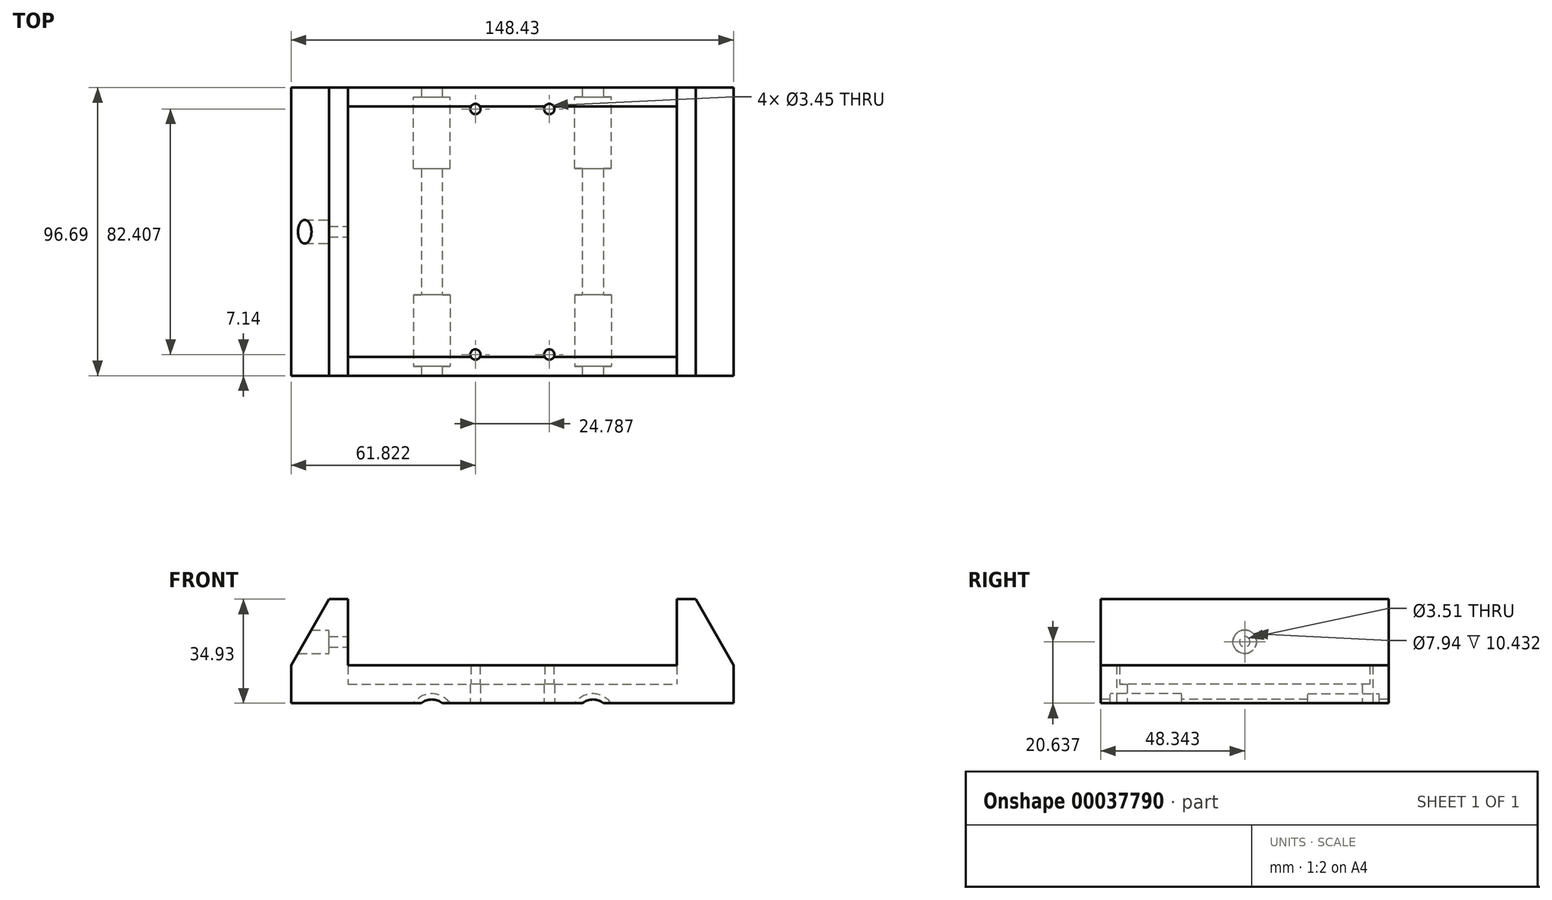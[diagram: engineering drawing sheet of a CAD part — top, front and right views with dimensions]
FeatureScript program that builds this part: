
annotation { "Feature Type Name" : "Feature", "Feature Type Description" : "" }
export const myFeature = defineFeature(function(context is Context, id is Id, definition is map)
    precondition{}
    {
        {
            var Q0;
            Q0=qCreatedBy(makeId("Top.planeOp"),FACE);
            var sketch = newSketch(context, id + "F0", { "sketchPlane" : qUnion([Q0])});
            skLineSegment(sketch, "E0.bottom", {"start": v(0, 0) * mm, "end": v(148.43, 0) * mm});
            skLineSegment(sketch, "E0.top", {"start": v(0, -96.7) * mm, "end": v(148.43, -96.7) * mm});
            skLineSegment(sketch, "E0.left", {"start": v(0, 0) * mm, "end": v(0, -96.7) * mm});
            skLineSegment(sketch, "E0.right", {"start": v(148.43, 0) * mm, "end": v(148.43, -96.7) * mm});
            skLineSegment(sketch, "E1", {"start": v(0, -48.35) * mm, "end": v(148.43, -48.35) * mm, "construction": true});
            skLineSegment(sketch, "E2.rect.bottom", {"start": v(61.82, -7.14) * mm, "end": v(86.6, -7.14) * mm, "construction": true});
            skLineSegment(sketch, "E2.rect.top", {"start": v(61.82, -89.55) * mm, "end": v(86.6, -89.55) * mm, "construction": true});
            skLineSegment(sketch, "E2.rect.left", {"start": v(61.82, -7.14) * mm, "end": v(61.82, -89.55) * mm, "construction": true});
            skLineSegment(sketch, "E2.rect.right", {"start": v(86.6, -7.14) * mm, "end": v(86.6, -89.55) * mm, "construction": true});
            skPoint(sketch, "E2.rect.middle", {"position": v(74.22, -48.35) * mm});
            skCircle(sketch, "E3", {"center": v(61.82, -7.14) * mm, "radius": 1.73 * mm});
            skCircle(sketch, "E4", {"center": v(86.6, -7.14) * mm, "radius": 1.73 * mm});
            skCircle(sketch, "E5", {"center": v(86.6, -89.55) * mm, "radius": 1.73 * mm});
            skCircle(sketch, "E6", {"center": v(61.82, -89.55) * mm, "radius": 1.73 * mm});
            skLineSegment(sketch, "E7", {"start": v(61.82, -7.14) * mm, "end": v(61.82, 0) * mm, "construction": true});
            skSolve(sketch);
        }
        {
            var Q0;
            Q0 = qSketchRegion(id + "F0", true);
            extrude(context, id + "F1", {"entities" : qUnion([Q0]), "depth" : 6.35 * mm});
        }
        {
            var Q0;
            Q0=makeQuery(id+"F1.opExtrude","CAP_FACE",FACE,{"disambiguationData":[OSD([sQuery(id+"F0.wireOp",EDGE,"E0.bottom"),sQuery(id+"F0.wireOp",EDGE,"E0.top"),sQuery(id+"F0.wireOp",EDGE,"E0.left"),sQuery(id+"F0.wireOp",EDGE,"E0.right")])],"isStart":false});
            var sketch = newSketch(context, id + "F2", { "sketchPlane" : qUnion([Q0])});
            skLineSegment(sketch, "E8.bottom", {"start": v(0, 0) * mm, "end": v(148.43, 0) * mm});
            skLineSegment(sketch, "E8.top", {"start": v(0, -96.7) * mm, "end": v(148.43, -96.7) * mm});
            skLineSegment(sketch, "E8.left", {"start": v(0, 0) * mm, "end": v(0, -96.7) * mm});
            skLineSegment(sketch, "E8.right", {"start": v(148.43, 0) * mm, "end": v(148.43, -96.7) * mm});
            skLineSegment(sketch, "E9.bottom", {"start": v(19.05, -6.35) * mm, "end": v(129.38, -6.35) * mm});
            skLineSegment(sketch, "E9.top", {"start": v(19.05, -90.34) * mm, "end": v(129.38, -90.34) * mm});
            skLineSegment(sketch, "E9.left", {"start": v(19.05, -6.35) * mm, "end": v(19.05, -90.34) * mm});
            skLineSegment(sketch, "E9.right", {"start": v(129.38, -6.35) * mm, "end": v(129.38, -90.34) * mm});
            skLineSegment(sketch, "E10", {"start": v(129.38, -48.35) * mm, "end": v(148.43, -48.35) * mm, "construction": true});
            skLineSegment(sketch, "E11", {"start": v(19.05, -48.35) * mm, "end": v(0, -48.35) * mm, "construction": true});
            skLineSegment(sketch, "E12", {"start": v(74.22, -6.35) * mm, "end": v(74.22, 0) * mm, "construction": true});
            skSolve(sketch);
        }
        {
            var Q0;
            Q0 = qSketchRegion(id + "F2", true);
            extrude(context, id + "F3", {"entities" : qUnion([Q0]), "operationType" : NewBodyOperationType.ADD, "depth" : 6.35 * mm});
        }
        {
            var Q0;
            Q0=makeQuery(id+"F3.opExtrude","CAP_FACE",FACE,{"disambiguationData":[OSD([sQuery(id+"F2.wireOp",EDGE,"E8.bottom"),sQuery(id+"F2.wireOp",EDGE,"E8.top"),sQuery(id+"F2.wireOp",EDGE,"E8.left"),sQuery(id+"F2.wireOp",EDGE,"E8.right"),sQuery(id+"F2.wireOp",EDGE,"E9.bottom"),sQuery(id+"F2.wireOp",EDGE,"E9.top"),sQuery(id+"F2.wireOp",EDGE,"E9.left"),sQuery(id+"F2.wireOp",EDGE,"E9.right")])],"isStart":false});
            var sketch = newSketch(context, id + "F4", { "sketchPlane" : qUnion([Q0])});
            skLineSegment(sketch, "E13.bottom", {"start": v(0, 0) * mm, "end": v(19.05, 0) * mm});
            skLineSegment(sketch, "E13.top", {"start": v(0, -96.7) * mm, "end": v(19.05, -96.7) * mm});
            skLineSegment(sketch, "E13.left", {"start": v(0, 0) * mm, "end": v(0, -96.7) * mm});
            skLineSegment(sketch, "E13.right", {"start": v(19.05, 0) * mm, "end": v(19.05, -96.7) * mm});
            skLineSegment(sketch, "E14.bottom", {"start": v(148.43, 0) * mm, "end": v(129.38, 0) * mm});
            skLineSegment(sketch, "E14.top", {"start": v(148.43, -96.7) * mm, "end": v(129.38, -96.7) * mm});
            skLineSegment(sketch, "E14.left", {"start": v(148.43, 0) * mm, "end": v(148.43, -96.7) * mm});
            skLineSegment(sketch, "E14.right", {"start": v(129.38, 0) * mm, "end": v(129.38, -96.7) * mm});
            skSolve(sketch);
        }
        {
            var Q0;
            Q0 = qSketchRegion(id + "F4", true);
            extrude(context, id + "F5", {"entities" : qUnion([Q0]), "operationType" : NewBodyOperationType.ADD, "depth" : 22.22 * mm});
        }
        {
            var Q0;
            Q0=makeQuery(id+"F5.opExtrude","CAP_EDGE",EDGE,{"disambiguationData":[OSD([sQuery(id+"F4.wireOp",EDGE,"E13.left")])],"isStart":false});
            chamfer(context, id + "F6", {"entities" : qUnion([Q0]), "chamferType" : ChamferType.TWO_OFFSETS, "width1" : 12.7 * mm, "oppositeDirection" : false, "width2" : 22.22 * mm, "tangentPropagation" : true});
        }
        {
            var Q0;
            Q0=makeQuery(id+"F5.opExtrude","CAP_EDGE",EDGE,{"disambiguationData":[OSD([sQuery(id+"F4.wireOp",EDGE,"E14.left")])],"isStart":false});
            chamfer(context, id + "F7", {"entities" : qUnion([Q0]), "chamferType" : ChamferType.TWO_OFFSETS, "width1" : 22.22 * mm, "oppositeDirection" : false, "width2" : 12.7 * mm, "tangentPropagation" : true});
        }
        {
            var Q0;
            Q0=makeQuery(id+"F5.boolean.opBoolean","MERGE",FACE,{"derivedFrom":[makeQuery(id+"F3.opExtrude","SWEPT_FACE",FACE,{"disambiguationData":[OSD([sQuery(id+"F2.wireOp",EDGE,"E9.left")])]}),makeQuery(id+"F5.opExtrude","SWEPT_FACE",FACE,{"disambiguationData":[OSD([sQuery(id+"F4.wireOp",EDGE,"E13.right")])]})]});
            var sketch = newSketch(context, id + "F8", { "sketchPlane" : qUnion([Q0])});
            skLineSegment(sketch, "E15", {"start": v(-48.35, 34.93) * mm, "end": v(-48.35, 6.35) * mm, "construction": true});
            skCircle(sketch, "E16", {"center": v(-48.35, 20.64) * mm, "radius": 1.75 * mm});
            skSolve(sketch);
        }
        {
            var Q0;
            Q0 = qSketchRegion(id + "F8", true);
            var Q1;
            Q1=makeQuery(id+"F6.opChamfer","BLEND_FACE",FACE,{"disambiguationData":[OSD([sQuery(id+"F4.wireOp",EDGE,"E13.left")])]});
            extrude(context, id + "F9", {"entities" : qUnion([Q0]), "operationType" : NewBodyOperationType.REMOVE, "endBound" : BoundingType.UP_TO_SURFACE, "oppositeDirection" : true, "endBoundEntityFace" : qUnion([Q1]), "depth" : 25.4 * mm});
        }
        {
            var Q0;
            Q0=makeQuery(id+"F5.boolean.opBoolean","MERGE",FACE,{"derivedFrom":[makeQuery(id+"F3.boolean.opBoolean","MERGE",FACE,{"derivedFrom":[makeQuery(id+"F1.opExtrude","SWEPT_FACE",FACE,{"disambiguationData":[OSD([sQuery(id+"F0.wireOp",EDGE,"E0.bottom")])]}),makeQuery(id+"F3.opExtrude","SWEPT_FACE",FACE,{"disambiguationData":[OSD([sQuery(id+"F2.wireOp",EDGE,"E8.bottom")])]})]}),makeQuery(id+"F5.opExtrude","SWEPT_FACE",FACE,{"disambiguationData":[OSD([sQuery(id+"F4.wireOp",EDGE,"E13.bottom")])]}),makeQuery(id+"F5.opExtrude","SWEPT_FACE",FACE,{"disambiguationData":[OSD([sQuery(id+"F4.wireOp",EDGE,"E14.bottom")])]})]});
            cPlane(context, id + "F10", {"entities" : qUnion([Q0]), "cplaneType" : CPlaneType.OFFSET, "offset" : 3.17 * mm, "oppositeDirection" : true, "width" : 152.4 * mm, "height" : 152.4 * mm});
        }
        {
            var Q0;
            Q0=qCreatedBy(id+"F10.planeOp",FACE);
            var sketch = newSketch(context, id + "F11", { "sketchPlane" : qUnion([Q0])});
            skLineSegment(sketch, "E17", {"start": v(-41.05, 0) * mm, "end": v(-53.3, 0) * mm});
            skArc(sketch, "E18", {"start": v(-41.05, 0) * mm, "mid": v(-47.18, 3.17) * mm, "end": v(-53.3, 0) * mm});
            skLineSegment(sketch, "E19", {"start": v(-107.38, 0) * mm, "end": v(-95.13, 0) * mm});
            skArc(sketch, "E20", {"start": v(-95.13, 0) * mm, "mid": v(-101.25, 3.17) * mm, "end": v(-107.38, 0) * mm});
            skLineSegment(sketch, "E21", {"start": v(-53.3, 0) * mm, "end": v(-95.13, 0) * mm, "construction": true});
            skPoint(sketch, "E22", {"position": v(-74.22, 0) * mm});
            skSolve(sketch);
        }
        {
            var Q0;
            Q0 = qSketchRegion(id + "F11", true);
            extrude(context, id + "F12", {"entities" : qUnion([Q0]), "operationType" : NewBodyOperationType.REMOVE, "oppositeDirection" : true, "depth" : 24 * mm});
        }
        {
            var Q0;
            Q0=makeQuery(id+"F5.boolean.opBoolean","MERGE",FACE,{"derivedFrom":[makeQuery(id+"F3.boolean.opBoolean","MERGE",FACE,{"derivedFrom":[makeQuery(id+"F1.opExtrude","SWEPT_FACE",FACE,{"disambiguationData":[OSD([sQuery(id+"F0.wireOp",EDGE,"E0.top")])]}),makeQuery(id+"F3.opExtrude","SWEPT_FACE",FACE,{"disambiguationData":[OSD([sQuery(id+"F2.wireOp",EDGE,"E8.top")])]})]}),makeQuery(id+"F5.opExtrude","SWEPT_FACE",FACE,{"disambiguationData":[OSD([sQuery(id+"F4.wireOp",EDGE,"E13.top")])]}),makeQuery(id+"F5.opExtrude","SWEPT_FACE",FACE,{"disambiguationData":[OSD([sQuery(id+"F4.wireOp",EDGE,"E14.top")])]})]});
            cPlane(context, id + "F13", {"entities" : qUnion([Q0]), "cplaneType" : CPlaneType.OFFSET, "offset" : 3.17 * mm, "oppositeDirection" : true, "width" : 152.4 * mm, "height" : 152.4 * mm});
        }
        {
            var Q0;
            Q0=qCreatedBy(id+"F13.planeOp",FACE);
            var sketch = newSketch(context, id + "F14", { "sketchPlane" : qUnion([Q0])});
            skLineSegment(sketch, "E23", {"start": v(41.05, 0) * mm, "end": v(53.3, 0) * mm});
            skLineSegment(sketch, "E24", {"start": v(95.13, 0) * mm, "end": v(107.38, 0) * mm});
            skArc(sketch, "E25", {"start": v(53.3, 0) * mm, "mid": v(47.18, 3.17) * mm, "end": v(41.05, 0) * mm});
            skArc(sketch, "E26", {"start": v(107.38, 0) * mm, "mid": v(101.25, 3.17) * mm, "end": v(95.13, 0) * mm});
            skSolve(sketch);
        }
        {
            var Q0;
            Q0 = qSketchRegion(id + "F14", true);
            extrude(context, id + "F15", {"entities" : qUnion([Q0]), "operationType" : NewBodyOperationType.REMOVE, "oppositeDirection" : true, "depth" : 24 * mm});
        }
        {
            var Q0;
            Q0=makeQuery(id+"F5.boolean.opBoolean","MERGE",FACE,{"derivedFrom":[makeQuery(id+"F3.opExtrude","SWEPT_FACE",FACE,{"disambiguationData":[OSD([sQuery(id+"F2.wireOp",EDGE,"E9.left")])]}),makeQuery(id+"F5.opExtrude","SWEPT_FACE",FACE,{"disambiguationData":[OSD([sQuery(id+"F4.wireOp",EDGE,"E13.right")])]})]});
            cPlane(context, id + "F16", {"entities" : qUnion([Q0]), "cplaneType" : CPlaneType.OFFSET, "offset" : 6.35 * mm, "oppositeDirection" : true, "width" : 152.4 * mm, "height" : 152.4 * mm});
        }
        {
            var Q0;
            Q0=qCreatedBy(id+"F16.planeOp",FACE);
            var sketch = newSketch(context, id + "F17", { "sketchPlane" : qUnion([Q0])});
            skCircle(sketch, "E27", {"center": v(-48.35, 20.64) * mm, "radius": 3.97 * mm});
            skSolve(sketch);
        }
        {
            var Q0;
            Q0 = qSketchRegion(id + "F17", true);
            var Q1;
            Q1=makeQuery(id+"F6.opChamfer","BLEND_FACE",FACE,{"disambiguationData":[OSD([sQuery(id+"F4.wireOp",EDGE,"E13.left")])]});
            extrude(context, id + "F18", {"entities" : qUnion([Q0]), "operationType" : NewBodyOperationType.REMOVE, "endBound" : BoundingType.UP_TO_SURFACE, "oppositeDirection" : true, "endBoundEntityFace" : qUnion([Q1]), "depth" : 25.4 * mm});
        }
        {
            var Q0;
            {var subQ0=sQuery(id+"F2.wireOp",EDGE,"E9.top");var subQ1=sQuery(id+"F0.wireOp",EDGE,"E6");Q0=makeQuery(id+"F3.boolean.opBoolean","SPLIT",FACE,{"disambiguationData":[TD([makeQuery(id+"F1.opExtrude","SWEPT_FACE",FACE,{"disambiguationData":[OSD([subQ1])]})])],"derivedFrom":makeQuery(id+"F3.opExtrude","CAP_FACE",FACE,{"disambiguationData":[OSD([sQuery(id+"F2.wireOp",EDGE,"E8.bottom"),sQuery(id+"F2.wireOp",EDGE,"E8.top"),sQuery(id+"F2.wireOp",EDGE,"E8.left"),sQuery(id+"F2.wireOp",EDGE,"E8.right"),sQuery(id+"F2.wireOp",EDGE,"E9.bottom"),subQ0,sQuery(id+"F2.wireOp",EDGE,"E9.left"),sQuery(id+"F2.wireOp",EDGE,"E9.right")])],"isStart":true})});}
            var Q1;
            {var subQ0=sQuery(id+"F2.wireOp",EDGE,"E9.top");var subQ1=sQuery(id+"F0.wireOp",EDGE,"E5");Q1=makeQuery(id+"F3.boolean.opBoolean","SPLIT",FACE,{"disambiguationData":[TD([makeQuery(id+"F1.opExtrude","SWEPT_FACE",FACE,{"disambiguationData":[OSD([subQ1])]})])],"derivedFrom":makeQuery(id+"F3.opExtrude","CAP_FACE",FACE,{"disambiguationData":[OSD([sQuery(id+"F2.wireOp",EDGE,"E8.bottom"),sQuery(id+"F2.wireOp",EDGE,"E8.top"),sQuery(id+"F2.wireOp",EDGE,"E8.left"),sQuery(id+"F2.wireOp",EDGE,"E8.right"),sQuery(id+"F2.wireOp",EDGE,"E9.bottom"),subQ0,sQuery(id+"F2.wireOp",EDGE,"E9.left"),sQuery(id+"F2.wireOp",EDGE,"E9.right")])],"isStart":true})});}
            var Q2;
            {var subQ0=sQuery(id+"F2.wireOp",EDGE,"E9.bottom");var subQ1=sQuery(id+"F0.wireOp",EDGE,"E4");Q2=makeQuery(id+"F3.boolean.opBoolean","SPLIT",FACE,{"disambiguationData":[TD([makeQuery(id+"F1.opExtrude","SWEPT_FACE",FACE,{"disambiguationData":[OSD([subQ1])]})])],"derivedFrom":makeQuery(id+"F3.opExtrude","CAP_FACE",FACE,{"disambiguationData":[OSD([sQuery(id+"F2.wireOp",EDGE,"E8.bottom"),sQuery(id+"F2.wireOp",EDGE,"E8.top"),sQuery(id+"F2.wireOp",EDGE,"E8.left"),sQuery(id+"F2.wireOp",EDGE,"E8.right"),subQ0,sQuery(id+"F2.wireOp",EDGE,"E9.top"),sQuery(id+"F2.wireOp",EDGE,"E9.left"),sQuery(id+"F2.wireOp",EDGE,"E9.right")])],"isStart":true})});}
            var Q3;
            {var subQ0=sQuery(id+"F2.wireOp",EDGE,"E9.bottom");var subQ1=sQuery(id+"F0.wireOp",EDGE,"E3");Q3=makeQuery(id+"F3.boolean.opBoolean","SPLIT",FACE,{"disambiguationData":[TD([makeQuery(id+"F1.opExtrude","SWEPT_FACE",FACE,{"disambiguationData":[OSD([subQ1])]})])],"derivedFrom":makeQuery(id+"F3.opExtrude","CAP_FACE",FACE,{"disambiguationData":[OSD([sQuery(id+"F2.wireOp",EDGE,"E8.bottom"),sQuery(id+"F2.wireOp",EDGE,"E8.top"),sQuery(id+"F2.wireOp",EDGE,"E8.left"),sQuery(id+"F2.wireOp",EDGE,"E8.right"),subQ0,sQuery(id+"F2.wireOp",EDGE,"E9.top"),sQuery(id+"F2.wireOp",EDGE,"E9.left"),sQuery(id+"F2.wireOp",EDGE,"E9.right")])],"isStart":true})});}
            var Q4;
            {var subQ0=sQuery(id+"F2.wireOp",EDGE,"E8.top");var subQ1=sQuery(id+"F2.wireOp",EDGE,"E9.top");var subQ2=sQuery(id+"F2.wireOp",EDGE,"E9.left");var subQ3=sQuery(id+"F2.wireOp",EDGE,"E9.right");Q4=makeQuery(id+"F5.boolean.opBoolean","SPLIT",FACE,{"disambiguationData":[TD([makeQuery(id+"F1.opExtrude","SWEPT_FACE",FACE,{"disambiguationData":[OSD([sQuery(id+"F0.wireOp",EDGE,"E0.top")])]})])],"derivedFrom":makeQuery(id+"F3.opExtrude","CAP_FACE",FACE,{"disambiguationData":[OSD([sQuery(id+"F2.wireOp",EDGE,"E8.bottom"),subQ0,sQuery(id+"F2.wireOp",EDGE,"E8.left"),sQuery(id+"F2.wireOp",EDGE,"E8.right"),sQuery(id+"F2.wireOp",EDGE,"E9.bottom"),subQ1,subQ2,subQ3])],"isStart":false})});}
            extrude(context, id + "F19", {"entities" : qUnion([Q0, Q1, Q2, Q3]), "operationType" : NewBodyOperationType.REMOVE, "endBound" : BoundingType.UP_TO_SURFACE, "oppositeDirection" : true, "endBoundEntityFace" : qUnion([Q4]), "depth" : 25.4 * mm});
        }
        {
            var Q0;
            Q0=makeQuery(id+"F5.boolean.opBoolean","MERGE",FACE,{"derivedFrom":[makeQuery(id+"F3.boolean.opBoolean","MERGE",FACE,{"derivedFrom":[makeQuery(id+"F1.opExtrude","SWEPT_FACE",FACE,{"disambiguationData":[OSD([sQuery(id+"F0.wireOp",EDGE,"E0.top")])]}),makeQuery(id+"F3.opExtrude","SWEPT_FACE",FACE,{"disambiguationData":[OSD([sQuery(id+"F2.wireOp",EDGE,"E8.top")])]})]}),makeQuery(id+"F5.opExtrude","SWEPT_FACE",FACE,{"disambiguationData":[OSD([sQuery(id+"F4.wireOp",EDGE,"E13.top")])]}),makeQuery(id+"F5.opExtrude","SWEPT_FACE",FACE,{"disambiguationData":[OSD([sQuery(id+"F4.wireOp",EDGE,"E14.top")])]})]});
            var sketch = newSketch(context, id + "F20", { "sketchPlane" : qUnion([Q0])});
            skCircle(sketch, "E28", {"center": v(47.18, -4.33) * mm, "radius": 5.59 * mm});
            skCircle(sketch, "E29", {"center": v(101.25, -4.33) * mm, "radius": 5.59 * mm});
            skSolve(sketch);
        }
        {
            var Q0;
            Q0 = qSketchRegion(id + "F20", true);
            var Q1;
            Q1=makeQuery(id+"F5.boolean.opBoolean","MERGE",FACE,{"derivedFrom":[makeQuery(id+"F3.boolean.opBoolean","MERGE",FACE,{"derivedFrom":[makeQuery(id+"F1.opExtrude","SWEPT_FACE",FACE,{"disambiguationData":[OSD([sQuery(id+"F0.wireOp",EDGE,"E0.bottom")])]}),makeQuery(id+"F3.opExtrude","SWEPT_FACE",FACE,{"disambiguationData":[OSD([sQuery(id+"F2.wireOp",EDGE,"E8.bottom")])]})]}),makeQuery(id+"F5.opExtrude","SWEPT_FACE",FACE,{"disambiguationData":[OSD([sQuery(id+"F4.wireOp",EDGE,"E13.bottom")])]}),makeQuery(id+"F5.opExtrude","SWEPT_FACE",FACE,{"disambiguationData":[OSD([sQuery(id+"F4.wireOp",EDGE,"E14.bottom")])]})]});
            extrude(context, id + "F21", {"entities" : qUnion([Q0]), "operationType" : NewBodyOperationType.REMOVE, "endBound" : BoundingType.UP_TO_SURFACE, "oppositeDirection" : true, "endBoundEntityFace" : qUnion([Q1]), "depth" : 25.4 * mm});
        }
    });
